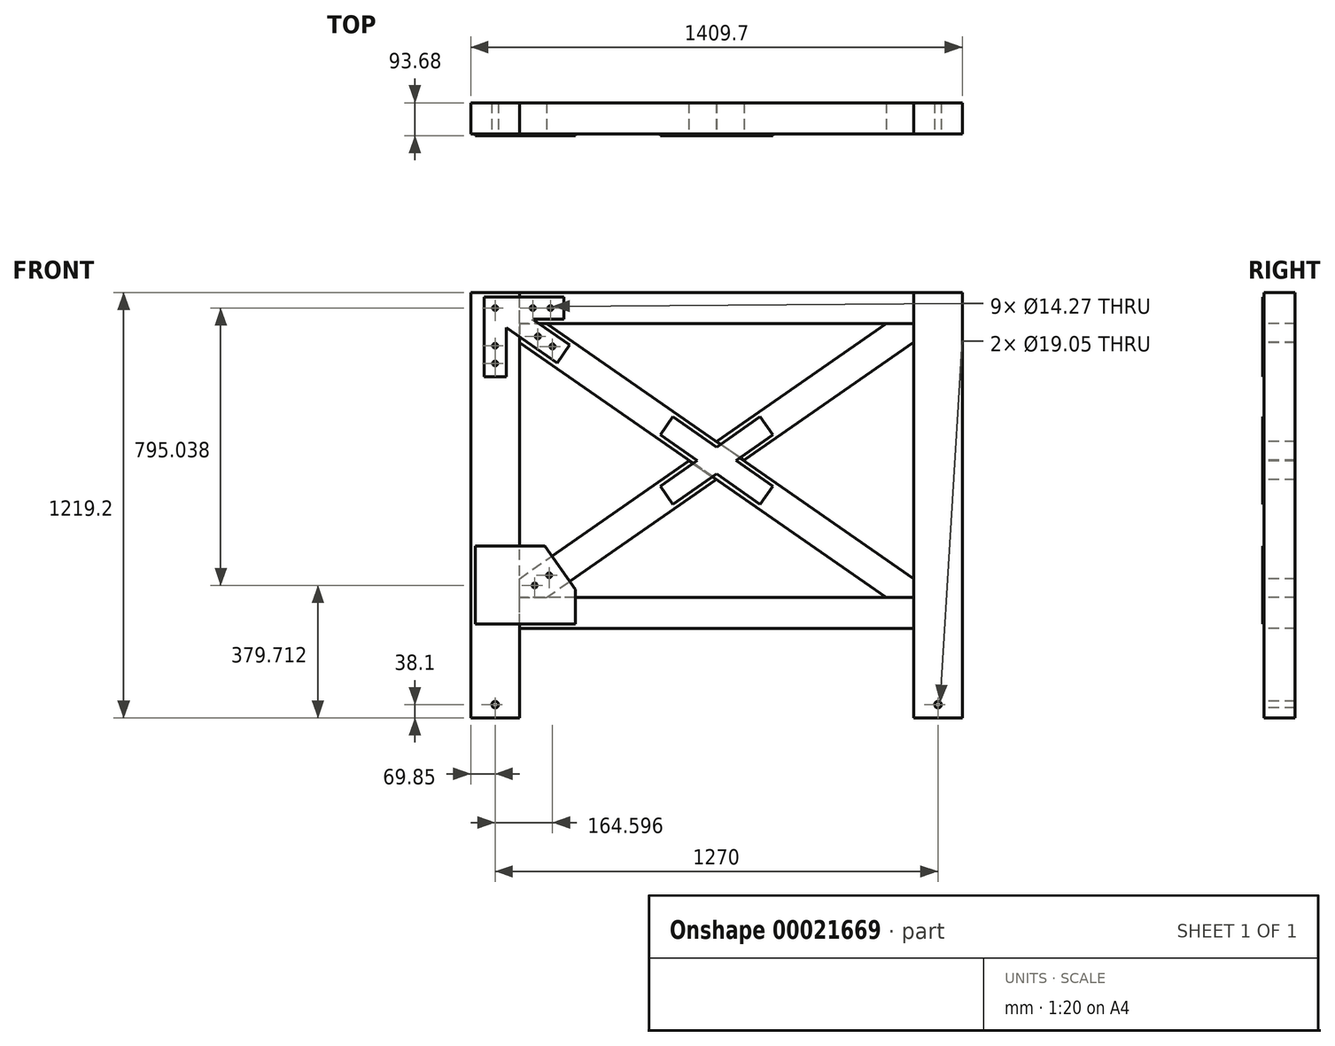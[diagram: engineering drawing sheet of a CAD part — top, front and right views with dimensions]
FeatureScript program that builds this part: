
annotation { "Feature Type Name" : "Feature", "Feature Type Description" : "" }
export const myFeature = defineFeature(function(context is Context, id is Id, definition is map)
    precondition{}
    {
        {
            var Q0;
            Q0=qCreatedBy(makeId("Top.planeOp"),FACE);
            var sketch = newSketch(context, id + "F0", { "sketchPlane" : qUnion([Q0])});
            skLineSegment(sketch, "E0.bottom", {"start": v(139.7, 0) * mm, "end": v(0, 0) * mm});
            skLineSegment(sketch, "E0.top", {"start": v(139.7, -88.9) * mm, "end": v(0, -88.9) * mm});
            skLineSegment(sketch, "E0.left", {"start": v(139.7, 0) * mm, "end": v(139.7, -88.9) * mm});
            skLineSegment(sketch, "E0.right", {"start": v(0, 0) * mm, "end": v(0, -88.9) * mm});
            skSolve(sketch);
        }
        {
            var Q0;
            Q0=makeQuery(id+"F0.imprint","IMPRINT",FACE,{"disambiguationData":[TD([[makeQuery(id+"F0.imprint","IMPRINT",EDGE,{"derivedFrom":sQuery(id+"F0.wireOp",EDGE,"E0.bottom")}),1.0]])]});
            extrude(context, id + "F1", {"entities" : qUnion([Q0]), "oppositeDirection" : true, "depth" : 1219.2 * mm});
        }
        {
            var Q0;
            Q0=makeQuery(id+"F1.opExtrude","SWEPT_FACE",FACE,{"disambiguationData":[OSD([sQuery(id+"F0.wireOp",EDGE,"E0.bottom")])]});
            var sketch = newSketch(context, id + "F2", { "sketchPlane" : qUnion([Q0])});
            skLineSegment(sketch, "E1", {"start": v(-69.85, -1219.2) * mm, "end": v(-69.85, -1181.1) * mm, "construction": true});
            skCircle(sketch, "E2", {"center": v(-69.85, -1181.1) * mm, "radius": 9.53 * mm});
            skSolve(sketch);
        }
        {
            var Q0;
            Q0=sQuery(id+"F2.wireOp",VERTEX,"E2.center");
            var Q1;
            Q1=makeQuery(id+"F1.opExtrude","SWEPT_BODY",BODY,{"disambiguationData":[OSD([sQuery(id+"F0.wireOp",EDGE,"E0.bottom"),sQuery(id+"F0.wireOp",EDGE,"E0.top"),sQuery(id+"F0.wireOp",EDGE,"E0.left"),sQuery(id+"F0.wireOp",EDGE,"E0.right")])]});
            hole(context, id + "F3", {"style" : HoleStyle.SIMPLE, "endStyle" : HoleEndStyle.THROUGH, "holeDiameter" : 19.05 * mm, "locations" : qUnion([Q0]), "scope" : qUnion([Q1]), "isTappedThrough" : true, "startStyle" : HoleStartStyle.PART});
        }
        {
            var Q0;
            Q0=makeQuery(id+"F1.opExtrude","SWEPT_FACE",FACE,{"disambiguationData":[OSD([sQuery(id+"F0.wireOp",EDGE,"E0.left")])]});
            var sketch = newSketch(context, id + "F4", { "sketchPlane" : qUnion([Q0])});
            skLineSegment(sketch, "E3", {"start": v(-44.45, 0) * mm, "end": v(-44.45, -44.45) * mm, "construction": true});
            skCircle(sketch, "E4", {"center": v(-44.45, -44.45) * mm, "radius": 6.35 * mm, "construction": true});
            skLineSegment(sketch, "E5", {"start": v(-44.45, -1219.2) * mm, "end": v(-44.45, -918.51) * mm, "construction": true});
            skCircle(sketch, "E6", {"center": v(-44.45, -918.51) * mm, "radius": 6.35 * mm, "construction": true});
            skLineSegment(sketch, "E7.bottom", {"start": v(-88.9, 0) * mm, "end": v(0, 0) * mm});
            skLineSegment(sketch, "E7.top", {"start": v(-88.9, -88.9) * mm, "end": v(0, -88.9) * mm});
            skLineSegment(sketch, "E7.left", {"start": v(-88.9, 0) * mm, "end": v(-88.9, -88.9) * mm});
            skLineSegment(sketch, "E7.right", {"start": v(0, 0) * mm, "end": v(0, -88.9) * mm});
            skLineSegment(sketch, "E8.bottom", {"start": v(0, -874.06) * mm, "end": v(-88.9, -874.06) * mm});
            skLineSegment(sketch, "E8.top", {"start": v(0, -962.96) * mm, "end": v(-88.9, -962.96) * mm});
            skLineSegment(sketch, "E8.left", {"start": v(0, -874.06) * mm, "end": v(0, -962.96) * mm});
            skLineSegment(sketch, "E8.right", {"start": v(-88.9, -874.06) * mm, "end": v(-88.9, -962.96) * mm});
            skSolve(sketch);
        }
        {
            var Q0;
            Q0=makeQuery(id+"F4.imprint","IMPRINT",FACE,{"disambiguationData":[TD([[makeQuery(id+"F4.imprint","IMPRINT",EDGE,{"derivedFrom":sQuery(id+"F4.wireOp",EDGE,"E7.bottom")}),1.0]])]});
            extrude(context, id + "F5", {"entities" : qUnion([Q0]), "depth" : 1130.3 * mm});
        }
        {
            var Q0;
            Q0=makeQuery(id+"F4.imprint","IMPRINT",FACE,{"disambiguationData":[TD([[makeQuery(id+"F4.imprint","IMPRINT",EDGE,{"derivedFrom":sQuery(id+"F4.wireOp",EDGE,"E8.bottom")}),1.0]])]});
            extrude(context, id + "F6", {"entities" : qUnion([Q0]), "depth" : 1130.3 * mm});
        }
        {
            var Q0;
            Q0=makeQuery(id+"F6.opExtrude","SWEPT_FACE",FACE,{"disambiguationData":[OSD([sQuery(id+"F4.wireOp",EDGE,"E8.right")])]});
            var sketch = newSketch(context, id + "F7", { "sketchPlane" : qUnion([Q0])});
            skLineSegment(sketch, "E9", {"start": v(1270, -874.06) * mm, "end": v(139.7, -88.9) * mm, "construction": true});
            skLineSegment(sketch, "E10.0", {"start": v(1270, -819.94) * mm, "end": v(217.61, -88.9) * mm});
            skLineSegment(sketch, "E11.0", {"start": v(1192.09, -874.06) * mm, "end": v(139.7, -143.02) * mm});
            skLineSegment(sketch, "E12", {"start": v(139.7, -88.9) * mm, "end": v(217.61, -88.9) * mm});
            skLineSegment(sketch, "E13", {"start": v(139.7, -88.9) * mm, "end": v(139.7, -143.02) * mm});
            skLineSegment(sketch, "E14", {"start": v(1270, -874.06) * mm, "end": v(1192.09, -874.06) * mm});
            skLineSegment(sketch, "E15", {"start": v(1270, -874.06) * mm, "end": v(1270, -819.94) * mm});
            skSolve(sketch);
        }
        {
            var Q0;
            Q0=makeQuery(id+"F7.imprint","IMPRINT",FACE,{"disambiguationData":[TD([[makeQuery(id+"F7.imprint","IMPRINT",EDGE,{"derivedFrom":sQuery(id+"F7.wireOp",EDGE,"ohj1r8rT-ciWI-mTj7-fBov-MIfJcJnKhdzf")}),1.0]])]});
            var Q1;
            Q1=makeQuery(id+"F7.imprint","IMPRINT",FACE,{"disambiguationData":[TD([[makeQuery(id+"F7.imprint","IMPRINT",EDGE,{"derivedFrom":sQuery(id+"F7.wireOp",EDGE,"E10.0")}),1.0]])]});
            extrude(context, id + "F8", {"entities" : qUnion([Q0, Q1]), "oppositeDirection" : true, "depth" : 88.9 * mm});
        }
        {
            var Q0;
            Q0=makeQuery(id+"F1.opExtrude","SWEPT_FACE",FACE,{"disambiguationData":[OSD([sQuery(id+"F0.wireOp",EDGE,"E0.top")])]});
            var sketch = newSketch(context, id + "F9", { "sketchPlane" : qUnion([Q0])});
            skLineSegment(sketch, "E16", {"start": v(139.7, -874.06) * mm, "end": v(704.85, -483.54) * mm, "construction": true});
            skLineSegment(sketch, "E17", {"start": v(139.7, -874.06) * mm, "end": v(1270, -88.9) * mm, "construction": true});
            skLineSegment(sketch, "E18.0", {"start": v(217.61, -874.06) * mm, "end": v(704.1, -536.13) * mm});
            skLineSegment(sketch, "E19.0", {"start": v(139.7, -819.94) * mm, "end": v(625.72, -482.33) * mm});
            skLineSegment(sketch, "E20", {"start": v(139.7, -874.06) * mm, "end": v(139.7, -819.94) * mm});
            skLineSegment(sketch, "E21", {"start": v(139.7, -874.06) * mm, "end": v(217.61, -874.06) * mm});
            skLineSegment(sketch, "E22", {"start": v(1270, -88.9) * mm, "end": v(1270, -142.93) * mm});
            skLineSegment(sketch, "E23", {"start": v(1270, -88.9) * mm, "end": v(1191.81, -88.9) * mm});
            skLineSegment(sketch, "E24", {"start": v(625.72, -482.33) * mm, "end": v(704.1, -536.13) * mm});
            skLineSegment(sketch, "E25", {"start": v(705.7, -426.58) * mm, "end": v(1191.81, -88.9) * mm});
            skLineSegment(sketch, "E26", {"start": v(784.26, -480.35) * mm, "end": v(1270, -142.93) * mm});
            skLineSegment(sketch, "E27", {"start": v(705.7, -426.58) * mm, "end": v(784.26, -480.35) * mm});
            skSolve(sketch);
        }
        {
            var Q0;
            Q0=makeQuery(id+"F9.imprint","IMPRINT",FACE,{"disambiguationData":[TD([[makeQuery(id+"F9.imprint","IMPRINT",EDGE,{"derivedFrom":sQuery(id+"F9.wireOp",EDGE,"E22")}),-1.0]])]});
            var Q1;
            Q1=makeQuery(id+"F9.imprint","IMPRINT",FACE,{"disambiguationData":[TD([[makeQuery(id+"F9.imprint","IMPRINT",EDGE,{"derivedFrom":sQuery(id+"F9.wireOp",EDGE,"E18.0")}),1.0]])]});
            extrude(context, id + "F10", {"entities" : qUnion([Q0, Q1]), "oppositeDirection" : true, "depth" : 88.9 * mm});
        }
        {
            var Q0;
            Q0=makeQuery(id+"F8.opExtrude","CAP_FACE",FACE,{"disambiguationData":[OSD([sQuery(id+"F7.wireOp",EDGE,"E10.0"),sQuery(id+"F7.wireOp",EDGE,"E11.0"),sQuery(id+"F7.wireOp",EDGE,"E12"),sQuery(id+"F7.wireOp",EDGE,"E13"),sQuery(id+"F7.wireOp",EDGE,"E14"),sQuery(id+"F7.wireOp",EDGE,"E15")])],"isStart":true});
            var sketch = newSketch(context, id + "F11", { "sketchPlane" : qUnion([Q0])});
            skLineSegment(sketch, "E28", {"start": v(0, 0) * mm, "end": v(0, -12.7) * mm, "construction": true});
            skLineSegment(sketch, "E29", {"start": v(0, 0) * mm, "end": v(38.1, 0) * mm, "construction": true});
            skLineSegment(sketch, "E30", {"start": v(38.1, -12.7) * mm, "end": v(38.1, -241.3) * mm});
            skLineSegment(sketch, "E31", {"start": v(38.1, -241.3) * mm, "end": v(101.6, -241.3) * mm});
            skLineSegment(sketch, "E32", {"start": v(101.6, -241.3) * mm, "end": v(101.6, -101.02) * mm});
            skLineSegment(sketch, "E33", {"start": v(101.6, -101.02) * mm, "end": v(247.62, -202.46) * mm});
            skLineSegment(sketch, "E34", {"start": v(247.62, -202.46) * mm, "end": v(283.85, -150.31) * mm});
            skLineSegment(sketch, "E35", {"start": v(283.85, -150.31) * mm, "end": v(177.17, -76.2) * mm});
            skLineSegment(sketch, "E36", {"start": v(177.17, -76.2) * mm, "end": v(266.7, -76.2) * mm});
            skLineSegment(sketch, "E37", {"start": v(266.7, -76.2) * mm, "end": v(266.7, -12.7) * mm});
            skLineSegment(sketch, "E38", {"start": v(266.7, -12.7) * mm, "end": v(38.1, -12.7) * mm});
            skLineSegment(sketch, "E39", {"start": v(265.74, -176.39) * mm, "end": v(1270, -874.06) * mm, "construction": true});
            skLineSegment(sketch, "E40.0", {"start": v(123.54, -116.26) * mm, "end": v(1251.89, -900.14) * mm, "construction": true});
            skLineSegment(sketch, "E41.0", {"start": v(159.77, -64.11) * mm, "end": v(1288.11, -847.99) * mm, "construction": true});
            skLineSegment(sketch, "E42.0", {"start": v(1263.65, -95.25) * mm, "end": v(1193.8, -95.25) * mm, "construction": true});
            skLineSegment(sketch, "E42.1", {"start": v(1263.65, -139.6) * mm, "end": v(1263.65, -95.25) * mm, "construction": true});
            skLineSegment(sketch, "E42.2", {"start": v(1193.8, -95.25) * mm, "end": v(716.89, -426.54) * mm, "construction": true});
            skLineSegment(sketch, "E42.3", {"start": v(716.89, -426.54) * mm, "end": v(784.23, -472.64) * mm, "construction": true});
            skLineSegment(sketch, "E42.4", {"start": v(784.23, -472.64) * mm, "end": v(1263.65, -139.6) * mm, "construction": true});
            skLineSegment(sketch, "E43", {"start": v(265.74, -176.39) * mm, "end": v(234.45, -154.65) * mm, "construction": true});
            skArc(sketch, "E44", {"start": v(101.6, -241.3) * mm, "mid": v(218.34, -192.94) * mm, "end": v(266.7, -76.2) * mm, "construction": true});
            skCircle(sketch, "E45", {"center": v(234.45, -154.65) * mm, "radius": 7.14 * mm});
            skLineSegment(sketch, "E46", {"start": v(234.45, -154.65) * mm, "end": v(192.65, -125.77) * mm, "construction": true});
            skCircle(sketch, "E47", {"center": v(192.65, -125.77) * mm, "radius": 7.14 * mm});
            skLineSegment(sketch, "E48", {"start": v(69.85, -241.3) * mm, "end": v(69.85, -203.2) * mm, "construction": true});
            skCircle(sketch, "E49", {"center": v(69.85, -203.2) * mm, "radius": 7.14 * mm});
            skLineSegment(sketch, "E50", {"start": v(69.85, -203.2) * mm, "end": v(69.85, -152.4) * mm, "construction": true});
            skCircle(sketch, "E51", {"center": v(69.85, -152.4) * mm, "radius": 7.14 * mm});
            skLineSegment(sketch, "E52", {"start": v(69.85, -152.4) * mm, "end": v(69.85, -44.45) * mm, "construction": true});
            skLineSegment(sketch, "E53", {"start": v(266.7, -44.45) * mm, "end": v(228.6, -44.45) * mm, "construction": true});
            skPoint(sketch, "E53.endSnap0", {"position": v(266.7, -44.45) * mm});
            skCircle(sketch, "E54", {"center": v(228.6, -44.45) * mm, "radius": 7.14 * mm});
            skLineSegment(sketch, "E55", {"start": v(228.6, -44.45) * mm, "end": v(69.85, -44.45) * mm, "construction": true});
            skCircle(sketch, "E56", {"center": v(69.85, -44.45) * mm, "radius": 7.14 * mm});
            skCircle(sketch, "E57.1.0.0", {"center": v(177.8, -44.45) * mm, "radius": 7.14 * mm});
            skLineSegment(sketch, "E57.direction1", {"start": v(228.6, -44.45) * mm, "end": v(177.8, -44.45) * mm, "construction": true});
            skSolve(sketch);
        }
        {
            var Q0;
            Q0 = qSketchRegion(id + "F11", true);
            extrude(context, id + "F12", {"entities" : qUnion([Q0]), "depth" : 4.76 * mm});
        }
        {
            var Q0;
            Q0=makeQuery(id+"F1.opExtrude","SWEPT_FACE",FACE,{"disambiguationData":[OSD([sQuery(id+"F0.wireOp",EDGE,"E0.top")])]});
            var sketch = newSketch(context, id + "F13", { "sketchPlane" : qUnion([Q0])});
            skLineSegment(sketch, "E58", {"start": v(69.85, -1219.2) * mm, "end": v(69.85, 0) * mm, "construction": true});
            skLineSegment(sketch, "E59", {"start": v(139.7, -918.51) * mm, "end": v(69.85, -918.51) * mm, "construction": true});
            skCircle(sketch, "E60", {"center": v(69.85, -918.51) * mm, "radius": 4.73 * mm, "construction": true});
            skSolve(sketch);
        }
        {
            var Q0;
            Q0=makeQuery(id+"F10.opExtrude","CAP_FACE",FACE,{"disambiguationData":[OSD([sQuery(id+"F9.wireOp",EDGE,"E22"),sQuery(id+"F9.wireOp",EDGE,"E23"),sQuery(id+"F9.wireOp",EDGE,"E25"),sQuery(id+"F9.wireOp",EDGE,"E26"),sQuery(id+"F9.wireOp",EDGE,"E27")])],"isStart":true});
            var sketch = newSketch(context, id + "F14", { "sketchPlane" : qUnion([Q0])});
            skLineSegment(sketch, "E61", {"start": v(1270, -874.06) * mm, "end": v(139.7, -88.9) * mm, "construction": true});
            skLineSegment(sketch, "E62", {"start": v(139.7, -874.06) * mm, "end": v(664.9, -509.23) * mm, "construction": true});
            skLineSegment(sketch, "E63", {"start": v(1270, -88.9) * mm, "end": v(664.9, -509.23) * mm, "construction": true});
            skLineSegment(sketch, "E64.0", {"start": v(866.24, -554.93) * mm, "end": v(760.5, -481.48) * mm});
            skLineSegment(sketch, "E65.0", {"start": v(830.01, -607.09) * mm, "end": v(704.85, -520.14) * mm});
            skLineSegment(sketch, "E66.0", {"start": v(830.01, -355.88) * mm, "end": v(704.85, -442.82) * mm});
            skLineSegment(sketch, "E67.0", {"start": v(866.24, -408.03) * mm, "end": v(760.5, -481.48) * mm});
            skLineSegment(sketch, "E68.0", {"start": v(579.69, -607.09) * mm, "end": v(704.85, -520.14) * mm});
            skLineSegment(sketch, "E69.0", {"start": v(543.46, -554.93) * mm, "end": v(646.8, -483.15) * mm});
            skLineSegment(sketch, "E70", {"start": v(543.46, -408.03) * mm, "end": v(579.69, -355.88) * mm});
            skLineSegment(sketch, "E71", {"start": v(866.24, -554.93) * mm, "end": v(830.01, -607.09) * mm});
            skLineSegment(sketch, "E72", {"start": v(543.46, -554.93) * mm, "end": v(579.69, -607.09) * mm});
            skLineSegment(sketch, "E73", {"start": v(830.01, -355.88) * mm, "end": v(866.24, -408.03) * mm});
            skLineSegment(sketch, "E74.trimOffspring", {"start": v(649.2, -481.48) * mm, "end": v(646.8, -483.15) * mm});
            skLineSegment(sketch, "E75.trimOffspring", {"start": v(649.2, -481.48) * mm, "end": v(543.46, -408.03) * mm});
            skLineSegment(sketch, "E76.trimOffspring", {"start": v(704.85, -442.82) * mm, "end": v(579.69, -355.88) * mm});
            skSolve(sketch);
        }
        {
            var Q0;
            Q0 = qSketchRegion(id + "F14", true);
            extrude(context, id + "F15", {"entities" : qUnion([Q0]), "depth" : 4.78 * mm});
        }
        {
            var Q0;
            Q0=makeQuery(id+"F1.opExtrude","SWEPT_FACE",FACE,{"disambiguationData":[OSD([sQuery(id+"F0.wireOp",EDGE,"E0.top")])]});
            var sketch = newSketch(context, id + "F16", { "sketchPlane" : qUnion([Q0])});
            skLineSegment(sketch, "E77", {"start": v(212.96, -726.45) * mm, "end": v(12.5, -726.45) * mm});
            skLineSegment(sketch, "E78", {"start": v(344.1, -677.95) * mm, "end": v(394.83, -750.96) * mm, "construction": true});
            skLineSegment(sketch, "E79", {"start": v(212.96, -726.45) * mm, "end": v(256.43, -789.03) * mm});
            skLineSegment(sketch, "E80", {"start": v(299.9, -851.61) * mm, "end": v(256.43, -789.03) * mm});
            skLineSegment(sketch, "E81", {"start": v(0, -845.96) * mm, "end": v(12.7, -845.96) * mm, "construction": true});
            skLineSegment(sketch, "E82", {"start": v(12.5, -726.45) * mm, "end": v(-0.2, -726.45) * mm, "construction": true});
            skLineSegment(sketch, "E83", {"start": v(219.26, -962.96) * mm, "end": v(219.26, -950.26) * mm, "construction": true});
            skLineSegment(sketch, "E84", {"start": v(256.43, -789.03) * mm, "end": v(367.62, -711.8) * mm, "construction": true});
            skLineSegment(sketch, "E85", {"start": v(256.43, -789.03) * mm, "end": v(224.92, -810.44) * mm, "construction": true});
            skCircle(sketch, "E86", {"center": v(224.92, -810.44) * mm, "radius": 7.14 * mm});
            skLineSegment(sketch, "E87", {"start": v(224.92, -810.44) * mm, "end": v(183.24, -839.49) * mm, "construction": true});
            skCircle(sketch, "E88", {"center": v(183.24, -839.49) * mm, "radius": 7.14 * mm});
            skLineSegment(sketch, "E89", {"start": v(299.9, -851.61) * mm, "end": v(299.9, -950.26) * mm});
            skLineSegment(sketch, "E90", {"start": v(299.9, -950.26) * mm, "end": v(219.26, -950.26) * mm});
            skLineSegment(sketch, "E91", {"start": v(219.26, -950.26) * mm, "end": v(12.7, -950.26) * mm});
            skLineSegment(sketch, "E92", {"start": v(139.7, -962.96) * mm, "end": v(139.7, -874.06) * mm, "construction": true});
            skLineSegment(sketch, "E93", {"start": v(139.7, -918.51) * mm, "end": v(-29.6, -918.51) * mm, "construction": true});
            skLineSegment(sketch, "E94", {"start": v(183.24, -839.49) * mm, "end": v(193.4, -854.08) * mm, "construction": true});
            skLineSegment(sketch, "E95", {"start": v(183.24, -839.49) * mm, "end": v(-25.61, -985.03) * mm, "construction": true});
            skLineSegment(sketch, "E96", {"start": v(12.5, -726.45) * mm, "end": v(12.7, -845.96) * mm});
            skLineSegment(sketch, "E97", {"start": v(12.7, -845.96) * mm, "end": v(12.7, -950.26) * mm});
            skLineSegment(sketch, "E98", {"start": v(0, -1219.2) * mm, "end": v(139.7, -1219.2) * mm, "construction": true});
            skLineSegment(sketch, "E99", {"start": v(139.7, -1219.2) * mm, "end": v(69.85, -1219.2) * mm, "construction": true});
            skLineSegment(sketch, "E100", {"start": v(69.85, -1219.2) * mm, "end": v(69.85, -918.5) * mm, "construction": true});
            skLineSegment(sketch, "E101", {"start": v(69.85, -918.51) * mm, "end": v(69.85, -918.5) * mm, "construction": true});
            skSolve(sketch);
        }
        {
            var Q0;
            Q0 = qSketchRegion(id + "F16", true);
            extrude(context, id + "F17", {"entities" : qUnion([Q0]), "depth" : 4.78 * mm, "offsetDistance" : 25.4 * mm});
        }
        {
            var Q0;
            Q0=makeQuery(id+"F1.opExtrude","SWEPT_BODY",BODY,{"disambiguationData":[OSD([sQuery(id+"F0.wireOp",EDGE,"E0.bottom"),sQuery(id+"F0.wireOp",EDGE,"E0.top"),sQuery(id+"F0.wireOp",EDGE,"E0.left"),sQuery(id+"F0.wireOp",EDGE,"E0.right")])]});
            transform(context, id + "F18", {"entities" : qUnion([Q0]), "transformType" : TransformType.TRANSLATION_3D, "dx" : 1270 * mm, "dy" : 0 * mm, "dz" : 0 * mm, "makeCopy" : true});
        }
    });
